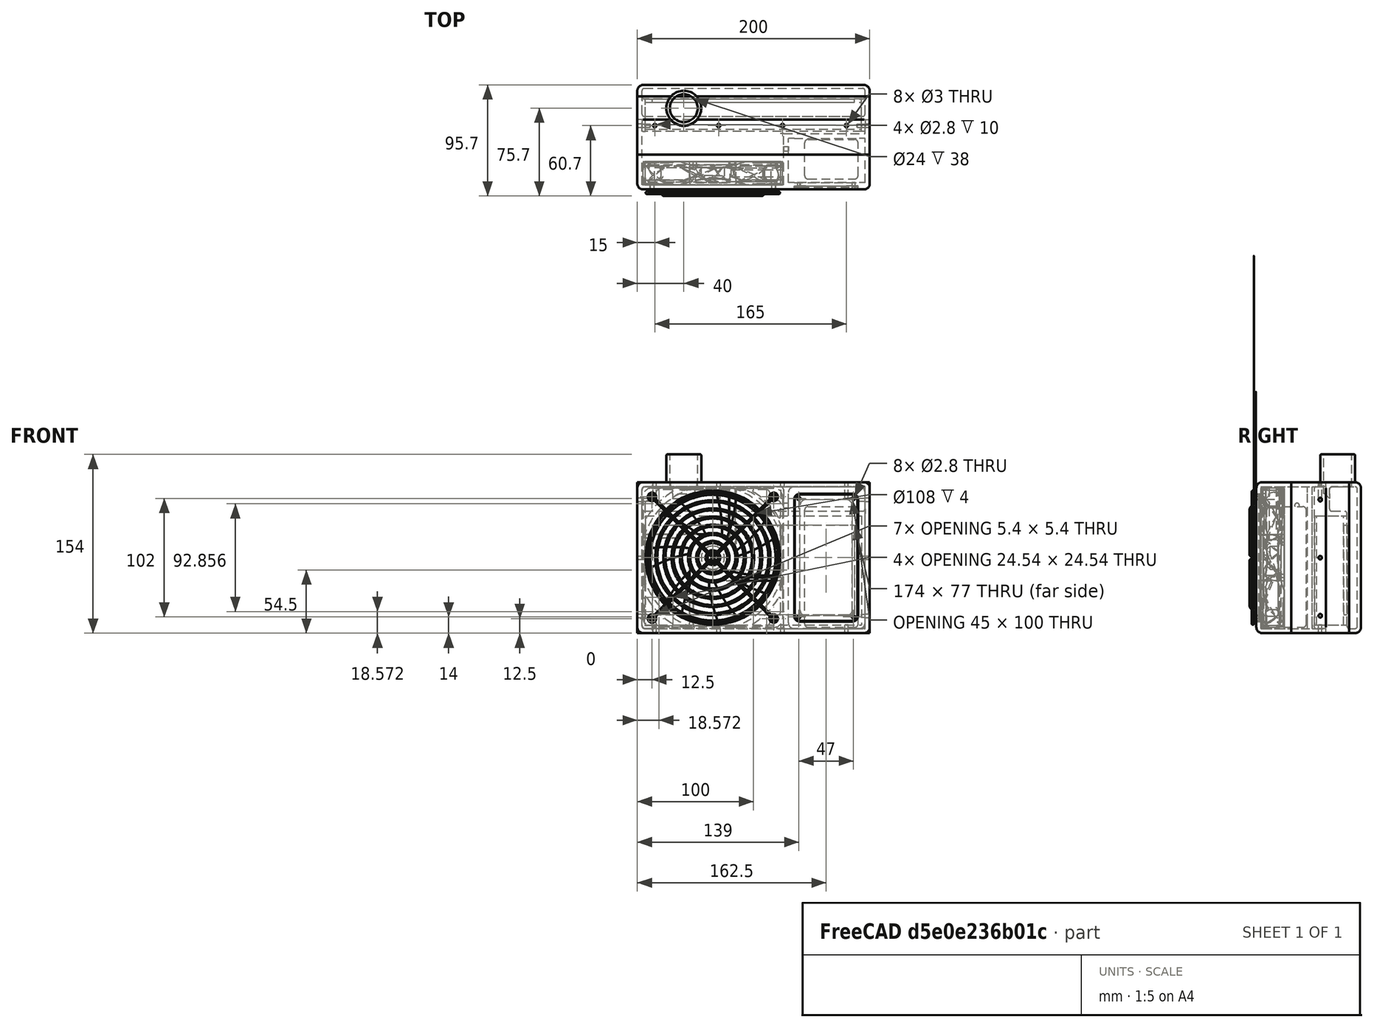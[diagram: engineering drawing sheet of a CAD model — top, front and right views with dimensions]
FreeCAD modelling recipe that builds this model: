
FCSTD DOCUMENT  (FreeCAD 0.16R6712 (Git))
Label: papr
License: All rights reserved
LicenseURL: http://en.wikipedia.org/wiki/All_rights_reserved
objects: Part::Cylinder×23, Part::Box×15, Part::Cut×13, Part::Feature×12, Part::MultiFuse×10, Part::Fillet×10, Sketcher::SketchObject×4, PartDesign::Pad×4, Part::Thickness×1, Part::Chamfer×1
note: 97 computed .brp shape members not serialized (recipe doc carries the construction recipe); baked Part::Feature solids carry a one-line shape summary decoded from their .brp

FEATURE [Part::Box] Box  label="Cube"
  Height = 94
  Length = 186
  Placement = pos=(7,52,7) rot=(0,0,1;0rad)
  Width = 26
FEATURE [Part::Feature] Part__Feature  label="Fan_Case"
  shape: bbox 130.3 x 20 x 130.3 mm, 716 faces (baked)
FEATURE [Part::Feature] Part__Feature001  label="Fan"
  Placement = pos=(0,-5,0) rot=(0,-1,0;0.339386rad)
  shape: bbox 152.3 x 17 x 155.7 mm, 53 faces (baked)
FEATURE [Part::Feature] Part__Feature002  label="rcofm-120_01"
  shape: bbox 115.6 x 231.2 x 3.6 mm, 4 faces (baked)
FEATURE [Part::Feature] Part__Feature003  label="rcofm-120_02"
  shape: bbox 12.6 x 25.2 x 3.6 mm, 4 faces (baked)
FEATURE [Part::Feature] Part__Feature004  label="rcofm-120_03"
  shape: bbox 85.1 x 170.2 x 3.6 mm, 4 faces (baked)
FEATURE [Part::Feature] Part__Feature005  label="rcofm-120_04"
  shape: bbox 42.68 x 85.36 x 3.6 mm, 4 faces (baked)
FEATURE [Part::Feature] Part__Feature006  label="rcofm-120_05"
  shape: bbox 56.82 x 113.6 x 3.6 mm, 4 faces (baked)
FEATURE [Part::Feature] Part__Feature007  label="rcofm-120_06"
  shape: bbox 28.54 x 57.08 x 3.6 mm, 4 faces (baked)
FEATURE [Part::Feature] Part__Feature008  label="rcofm-120_07"
  shape: bbox 114.6 x 58.13 x 7.204 mm, 36 faces (baked)
FEATURE [Part::Feature] Part__Feature009  label="rcofm-120_08"
  shape: bbox 114.6 x 58.12 x 7.204 mm, 36 faces (baked)
FEATURE [Part::Feature] Part__Feature010  label="rcofm-120_09"
  shape: bbox 70.96 x 141.9 x 3.6 mm, 4 faces (baked)
FEATURE [Part::Feature] Part__Feature011  label="rcofm-120_10"
  shape: bbox 99.24 x 198.5 x 3.6 mm, 4 faces (baked)
FEATURE [Part::MultiFuse] Fusion
  Placement = pos=(65,-3,65) rot=(1,0,0;1.5708rad)
  Shapes = -> [Part__Feature002,Part__Feature006,Part__Feature007,Part__Feature011,Part__Feature005,Part__Feature009,Part__Feature003,Part__Feature004,Part__Feature008,Part__Feature010]
FEATURE [Part::MultiFuse] Fusion001
  Placement = pos=(65,14,65) rot=(1,0,0;3.14159rad)
  Shapes = -> [Part__Feature,Part__Feature001]
FEATURE [Part::Box] Box001  label="Cube001"
  Height = 130
  Length = 200
  Placement = pos=(0,30,0) rot=(0,0,1;0rad)
  Width = 50
FEATURE [Part::Box] Box002  label="Cube002"
  Height = 130
  Length = 200
  Placement = pos=(0,50,0) rot=(0,0,1;0rad)
  Width = 40
FEATURE [Sketcher::SketchObject] Sketch
  sketch-geometry (4):
    g0: LineSegment StartX=0 StartY=60 StartZ=0 EndX=0 EndY=0 EndZ=0
    g1: LineSegment StartX=0 StartY=0 StartZ=0 EndX=200 EndY=0 EndZ=0
    g2: LineSegment StartX=200 StartY=0 StartZ=0 EndX=200 EndY=60 EndZ=0
    g3: LineSegment StartX=200 StartY=60 StartZ=0 EndX=0 EndY=60 EndZ=0
  constraints (11):
    c: Vertical(g0)
    c: Coincident(g0,g1)
    c: Horizontal(g1)
    c: Coincident(g2,g3)
    c: Coincident(g3,g0)
    c: Horizontal(g3)
    c: Vertical(g2)
    c: Distance(g3) = 200
    c: Coincident(g0,g-1)
    c: Distance(g0) = 60
    c: Coincident(g2,g1)
FEATURE [PartDesign::Pad] Pad
  Length = 130
  Length2 = 100
  Sketch = -> Sketch
  Type = 0
FEATURE [Sketcher::SketchObject] Sketch001
  Placement = pos=(0,-50,0) rot=(1,0,0;1.5708rad)
  sketch-geometry (9):
    g0: Circle CenterX=65 CenterY=65 CenterZ=0 NormalX=0 NormalY=0 NormalZ=1 Radius=54
    g1: LineSegment [constr] StartX=12.65 StartY=117.4 StartZ=0 EndX=117.4 EndY=117.4 EndZ=0
    g2: LineSegment [constr] StartX=117.4 StartY=117.4 StartZ=0 EndX=117.4 EndY=12.65 EndZ=0
    g3: LineSegment [constr] StartX=117.4 StartY=12.65 StartZ=0 EndX=12.65 EndY=12.65 EndZ=0
    g4: LineSegment [constr] StartX=12.65 StartY=12.65 StartZ=0 EndX=12.65 EndY=117.4 EndZ=0
    g5: Circle CenterX=12.65 CenterY=117.4 CenterZ=0 NormalX=0 NormalY=0 NormalZ=1 Radius=2
    g6: Circle CenterX=117.4 CenterY=117.4 CenterZ=0 NormalX=0 NormalY=0 NormalZ=1 Radius=2
    g7: Circle CenterX=117.4 CenterY=12.65 CenterZ=0 NormalX=0 NormalY=0 NormalZ=1 Radius=2
    g8: Circle CenterX=12.65 CenterY=12.65 CenterZ=0 NormalX=0 NormalY=0 NormalZ=1 Radius=2
  constraints (23):
    c: Coincident(g1,g2)
    c: Coincident(g2,g3)
    c: Coincident(g3,g4)
    c: Coincident(g4,g1)
    c: Horizontal(g1)
    c: Horizontal(g3)
    c: Vertical(g2)
    c: Vertical(g4)
    c: Coincident(g5,g1)
    c: Coincident(g6,g1)
    c: Coincident(g7,g2)
    c: Coincident(g8,g3)
    c: Radius(g8) = 2
    c: Equal(g8,g5)
    c: Equal(g8,g6)
    c: Equal(g8,g7)
    c: Equal(g1,g4)
    c: DistanceY(g-1,g3) = 12.65
    c: DistanceX(g-1,g3) = 12.65
    c: Distance(g4) = 104.75
    c: DistanceX(g-1,g0) = 65
    c: DistanceY(g-1,g0) = 65
    c: Radius(g0) = 54
FEATURE [PartDesign::Pad] Pad001
  Length = 100
  Length2 = 100
  Placement = pos=(0,-50,0) rot=(1,0,0;1.5708rad)
  Reversed = true
  Sketch = -> Sketch001
  Type = 0
FEATURE [Part::Box] Box003  label="Cube003"
  Height = 122
  Length = 66
  Placement = pos=(130,6,4) rot=(0,0,1;0rad)
  Width = 38
FEATURE [Part::Box] Box004  label="Cube004"
  Height = 110
  Length = 55
  Placement = pos=(135,-37,10) rot=(0,0,1;0rad)
  Width = 40
FEATURE [Part::Fillet] Fillet001
  Base = -> Box004
  Edges = 4 edges r=5: [Edge2,Edge4,Edge6,Edge8]
FEATURE [Part::Box] Box005  label="Cube005"
  Height = 100
  Length = 45
  Placement = pos=(140,-15,15) rot=(0,0,1;0rad)
  Width = 40
FEATURE [Part::MultiFuse] Fusion002
  Shapes = -> [Fillet001,Box005]
FEATURE [Part::Cut] Cut
  Base = -> Pad
  Tool = -> Fusion002
FEATURE [Part::Cut] Cut001
  Base = -> Cut
  Tool = -> Box003
FEATURE [Part::Fillet] Fillet
  Base = -> Cut001
  Edges = 4 edges r=5: [Edge41,Edge43,Edge45,Edge46]
FEATURE [Part::Fillet] Fillet002
  Base = -> Fillet
  Edges = 12 edges r=5: [Edge53,Edge54,Edge55,Edge56,Edge57,Edge59,Edge60,Edge62,Edge66,Edge67,Edge68,Edge70]
FEATURE [Part::Cylinder] Cylinder
  Angle = 360
  Height = 30
  Placement = pos=(120,35,110) rot=(0,1,0;1.5708rad)
  Radius = 2
FEATURE [Part::Box] Box006  label="Cube006"
  Height = 122
  Length = 122
  Placement = pos=(4,4,4) rot=(0,0,1;0rad)
  Width = 50
FEATURE [Part::Box] Box007  label="Cube007"
  Height = 104
  Length = 46
  Width = 34
FEATURE [Part::Box] Box008  label="Cube008"
  Height = 122
  Length = 192
  Placement = pos=(4,48,4) rot=(0,0,1;0rad)
  Width = 50
FEATURE [Part::MultiFuse] Fusion003
  Shapes = -> [Box006,Box008]
FEATURE [Part::Cut] Cut002
  Base = -> Fillet002
  Tool = -> Fusion003
FEATURE [Part::Cut] Cut003
  Base = -> Cut002
  Tool = -> Cylinder
FEATURE [Part::Fillet] Fillet003
  Base = -> Cut003
  Edges = 4 edges r=3: [Edge60,Edge63,Edge81,Edge89]
FEATURE [Part::Cut] Cut004
  Base = -> Fillet003
  Tool = -> Pad001
FEATURE [Part::Fillet] Fillet004
  Base = -> Box007
  Edges = 12 edges r=3: [Edge1,Edge2,Edge3,Edge4,Edge5,Edge6,Edge7,Edge8,Edge9,Edge10,Edge11,Edge12]
  Placement = pos=(144,9,5) rot=(0,0,1;0rad)
FEATURE [Sketcher::SketchObject] Sketch002
  Placement = pos=(0,-10,0) rot=(1,0,0;1.5708rad)
  sketch-geometry (8):
    g0: LineSegment [constr] StartX=139 StartY=116 StartZ=0 EndX=186 EndY=116 EndZ=0
    g1: LineSegment [constr] StartX=186 StartY=116 StartZ=0 EndX=186 EndY=14 EndZ=0
    g2: LineSegment [constr] StartX=186 StartY=14 StartZ=0 EndX=139 EndY=14 EndZ=0
    g3: LineSegment [constr] StartX=139 StartY=14 StartZ=0 EndX=139 EndY=116 EndZ=0
    g4: Circle CenterX=139 CenterY=116 CenterZ=0 NormalX=0 NormalY=0 NormalZ=1 Radius=1.4
    g5: Circle CenterX=186 CenterY=116 CenterZ=0 NormalX=0 NormalY=0 NormalZ=1 Radius=1.4
    g6: Circle CenterX=139 CenterY=14 CenterZ=0 NormalX=0 NormalY=0 NormalZ=1 Radius=1.4
    g7: Circle CenterX=186 CenterY=14 CenterZ=0 NormalX=0 NormalY=0 NormalZ=1 Radius=1.4
  constraints (20):
    c: Coincident(g0,g1)
    c: Coincident(g1,g2)
    c: Coincident(g2,g3)
    c: Coincident(g3,g0)
    c: Horizontal(g0)
    c: Horizontal(g2)
    c: Vertical(g1)
    c: Vertical(g3)
    c: Coincident(g4,g0)
    c: Coincident(g5,g0)
    c: Coincident(g6,g2)
    c: Coincident(g7,g1)
    c: Radius(g4) = 1.4
    c: Equal(g4,g5)
    c: Equal(g4,g6)
    c: Equal(g4,g7)
    c: DistanceX(g-1,g2) = 139
    c: DistanceY(g-1,g2) = 14
    c: Distance(g1) = 102
    c: Distance(g0) = 47
FEATURE [PartDesign::Pad] Pad002
  Length = 25
  Length2 = 100
  Placement = pos=(0,-10,0) rot=(1,0,0;1.5708rad)
  Reversed = true
  Sketch = -> Sketch002
  Type = 0
FEATURE [Part::Cut] Cut005
  Base = -> Cut004
  Tool = -> Pad002
FEATURE [Part::Box] Box009  label="Cube009"
  Height = 77
  Length = 174
  Placement = pos=(13,75,16) rot=(0,0,1;0rad)
  Width = 10
FEATURE [Part::Box] Box010  label="Cube010"
  Height = 122
  Length = 192
  Placement = pos=(4,82,4) rot=(0,0,1;0rad)
  Width = 9
FEATURE [Part::Box] Box011  label="Cube011"
  Height = 94
  Length = 186
  Placement = pos=(7,45,7) rot=(0,0,1;0rad)
  Width = 34
FEATURE [Part::Fillet] Fillet005
  Base = -> Box002
  Edges = 8 edges r=5: [Edge2,Edge3,Edge4,Edge6,Edge7,Edge8,Edge11,Edge12]
FEATURE [Part::Cylinder] Cylinder001
  Angle = 360
  Height = 28
  Placement = pos=(40,70,126) rot=(0,0,1;0rad)
  Radius = 15
FEATURE [Part::Cylinder] Cylinder002
  Angle = 360
  Height = 40
  Placement = pos=(40,70,120) rot=(0,0,1;0rad)
  Radius = 12
FEATURE [Part::Box] Box012  label="Cube012"
  Height = 21
  Length = 192
  Placement = pos=(4,67,105) rot=(0,0,1;0rad)
  Width = 19
FEATURE [Part::MultiFuse] Fusion004
  Placement = pos=(0,-4,0) rot=(0,0,1;0rad)
  Shapes = -> [Box012,Box011,Box010,Box009]
FEATURE [Part::Cut] Cut006
  Base = -> Fillet005
  Tool = -> Fusion004
FEATURE [Part::Cylinder] Cylinder003
  Angle = 360
  Height = 140
  Placement = pos=(15,0,-5) rot=(0,0,1;0rad)
  Radius = 1.5
FEATURE [Part::Cylinder] Cylinder004
  Angle = 360
  Height = 140
  Placement = pos=(180,0,-5) rot=(0,0,1;0rad)
  Radius = 1.5
FEATURE [Part::Cylinder] Cylinder005
  Angle = 360
  Height = 140
  Placement = pos=(70,0,-5) rot=(0,0,1;0rad)
  Radius = 1.5
FEATURE [Part::Cylinder] Cylinder006
  Angle = 360
  Height = 140
  Placement = pos=(125,0,-5) rot=(0,0,1;0rad)
  Radius = 1.5
FEATURE [Part::Cylinder] Cylinder007
  Angle = 360
  Height = 210
  Placement = pos=(-5,0,15) rot=(0,1,0;1.5708rad)
  Radius = 1.5
FEATURE [Part::MultiFuse] Fusion005
  Shapes = -> [Cylinder003,Cylinder004,Cylinder006,Cylinder005]
FEATURE [Part::Cylinder] Cylinder008
  Angle = 360
  Height = 210
  Placement = pos=(-5,0,115) rot=(0,1,0;1.5708rad)
  Radius = 1.5
FEATURE [Part::Cylinder] Cylinder009
  Angle = 360
  Height = 210
  Placement = pos=(-5,0,65) rot=(0,1,0;1.5708rad)
  Radius = 1.5
FEATURE [Part::MultiFuse] Fusion006
  Shapes = -> [Cylinder007,Cylinder008,Cylinder009]
FEATURE [Part::MultiFuse] Fusion007
  Placement = pos=(0,55,0) rot=(0,0,1;0rad)
  Shapes = -> [Fusion005,Fusion006]
FEATURE [Part::Cut] Cut007
  Base = -> Cut005
  Tool = -> Fusion007
FEATURE [Sketcher::SketchObject] Sketch003
  Placement = pos=(0,-10,0) rot=(1,0,0;1.5708rad)
  sketch-geometry (8):
    g0: LineSegment [constr] StartX=139 StartY=116 StartZ=0 EndX=186 EndY=116 EndZ=0
    g1: LineSegment [constr] StartX=186 StartY=116 StartZ=0 EndX=186 EndY=14 EndZ=0
    g2: LineSegment [constr] StartX=186 StartY=14 StartZ=0 EndX=139 EndY=14 EndZ=0
    g3: LineSegment [constr] StartX=139 StartY=14 StartZ=0 EndX=139 EndY=116 EndZ=0
    g4: Circle CenterX=139 CenterY=116 CenterZ=0 NormalX=0 NormalY=0 NormalZ=1 Radius=1.4
    g5: Circle CenterX=186 CenterY=116 CenterZ=0 NormalX=0 NormalY=0 NormalZ=1 Radius=1.4
    g6: Circle CenterX=139 CenterY=14 CenterZ=0 NormalX=0 NormalY=0 NormalZ=1 Radius=1.4
    g7: Circle CenterX=186 CenterY=14 CenterZ=0 NormalX=0 NormalY=0 NormalZ=1 Radius=1.4
  constraints (20):
    c: Coincident(g0,g1)
    c: Coincident(g1,g2)
    c: Coincident(g2,g3)
    c: Coincident(g3,g0)
    c: Horizontal(g0)
    c: Horizontal(g2)
    c: Vertical(g1)
    c: Vertical(g3)
    c: Coincident(g4,g0)
    c: Coincident(g5,g0)
    c: Coincident(g6,g2)
    c: Coincident(g7,g1)
    c: Radius(g4) = 1.4
    c: Equal(g4,g5)
    c: Equal(g4,g6)
    c: Equal(g4,g7)
    c: DistanceX(g-1,g2) = 139
    c: DistanceY(g-1,g2) = 14
    c: Distance(g1) = 102
    c: Distance(g0) = 47
FEATURE [Part::Box] Box013  label="Cube013"
  Height = 109
  Length = 54
  Placement = pos=(135.5,0,10.5) rot=(0,0,1;0rad)
  Width = 2
FEATURE [Part::Fillet] Fillet006
  Base = -> Box013
  Edges = 4 edges r=5: [Edge2,Edge4,Edge6,Edge8]
FEATURE [PartDesign::Pad] Pad003
  Length = 30
  Length2 = 100
  Placement = pos=(0,-10,0) rot=(1,0,0;1.5708rad)
  Reversed = true
  Sketch = -> Sketch003
  Type = 0
FEATURE [Part::Cut] Cut008
  Base = -> Fillet006
  Tool = -> Pad003
FEATURE [Part::Box] Box014  label="Cube014"
  Height = 134
  Length = 204
  Placement = pos=(-2,48,-2) rot=(0,0,1;0rad)
  Width = 20
FEATURE [Part::Thickness] Thickness
  Faces = -> Box014 [Face3,Face4]
  Intersection = false
  Join = 0
  Mode = 0
  SelfIntersection = false
  Value = -6
FEATURE [Part::Fillet] Fillet007
  Base = -> Thickness
  Edges = 4 edges r=3: [Edge17,Edge19,Edge23,Edge24]
  Placement = pos=(0,-8,0) rot=(0,0,1;0rad)
FEATURE [Part::Cut] Cut009
  Base = -> Cut006
  Tool = -> Fillet007
FEATURE [Part::Cylinder] Cylinder010
  Angle = 360
  Height = 28
  Placement = pos=(40,70,124) rot=(0,0,1;0rad)
  Radius = 15.2
FEATURE [Part::MultiFuse] Fusion008
  Shapes = -> [Cylinder001,Cut009]
FEATURE [Part::Cut] Cut010
  Base = -> Fusion008
  Tool = -> Cylinder002
FEATURE [Part::Cut] Cut011
  Base = -> Cut007
  Tool = -> Cylinder010
FEATURE [Part::Cylinder] Cylinder011
  Angle = 360
  Height = 140
  Placement = pos=(15,55,116) rot=(0,0,1;0rad)
  Radius = 1.4
FEATURE [Part::Cylinder] Cylinder013
  Angle = 360
  Height = 140
  Placement = pos=(70,55,116) rot=(0,0,1;0rad)
  Radius = 1.4
FEATURE [Part::Cylinder] Cylinder014
  Angle = 360
  Height = 140
  Placement = pos=(125,55,116) rot=(0,0,1;0rad)
  Radius = 1.4
FEATURE [Part::Cylinder] Cylinder015
  Angle = 360
  Height = 210
  Placement = pos=(-5,55,15) rot=(0,1,0;1.5708rad)
  Radius = 1.4
FEATURE [Part::Cylinder] Cylinder016
  Angle = 360
  Height = 16
  Placement = pos=(-5,55,115) rot=(0,1,0;1.5708rad)
  Radius = 1.4
FEATURE [Part::Cylinder] Cylinder017
  Angle = 360
  Height = 210
  Placement = pos=(-5,55,65) rot=(0,1,0;1.5708rad)
  Radius = 1.4
FEATURE [Part::Cylinder] Cylinder018 .. Cylinder021  x4 (patterned run collapsed; names and placements below)
  Angle = 360
  Height = 16
  Radius = 1.4
  placements: 4 in arithmetic series — first pos=(15,55,-5) rot=(0,0,1;0rad), step (55,0,0), last pos=(180,55,-5) rot=(0,0,1;0rad)
FEATURE [Part::Cylinder] Cylinder022
  Angle = 360
  Height = 210
  Placement = pos=(189,55,115) rot=(0,1,0;1.5708rad)
  Radius = 1.4
FEATURE [Part::Cylinder] Cylinder012
  Angle = 360
  Height = 140
  Placement = pos=(180,55,116) rot=(0,0,1;0rad)
  Radius = 1.4
FEATURE [Part::MultiFuse] Fusion009
  Shapes = -> [Cylinder015,Cylinder017,Cylinder016,Cylinder022,Cylinder011,Cylinder018,Cylinder013,Cylinder020,Cylinder014,Cylinder019,Cylinder021,Cylinder012]
FEATURE [Part::Cut] Cut012
  Base = -> Cut010
  Tool = -> Fusion009
FEATURE [Part::Fillet] Fillet008
  Base = -> Cut012
  Edges = 2 edges r=1: [Edge1,Edge66]
FEATURE [Part::Chamfer] Chamfer
  Base = -> Fillet008
  Edges = 1 edges r=4: [Edge24]
FEATURE [Part::Fillet] Fillet009
  Base = -> Chamfer
  Edges = 19 edges r=2: [Edge14,Edge15,Edge16,Edge17,Edge18,Edge19,Edge20,Edge21,Edge23,Edge24,Edge25,Edge26,Edge27,Edge28,Edge29,Edge30,Edge31,Edge32,Edge35]
